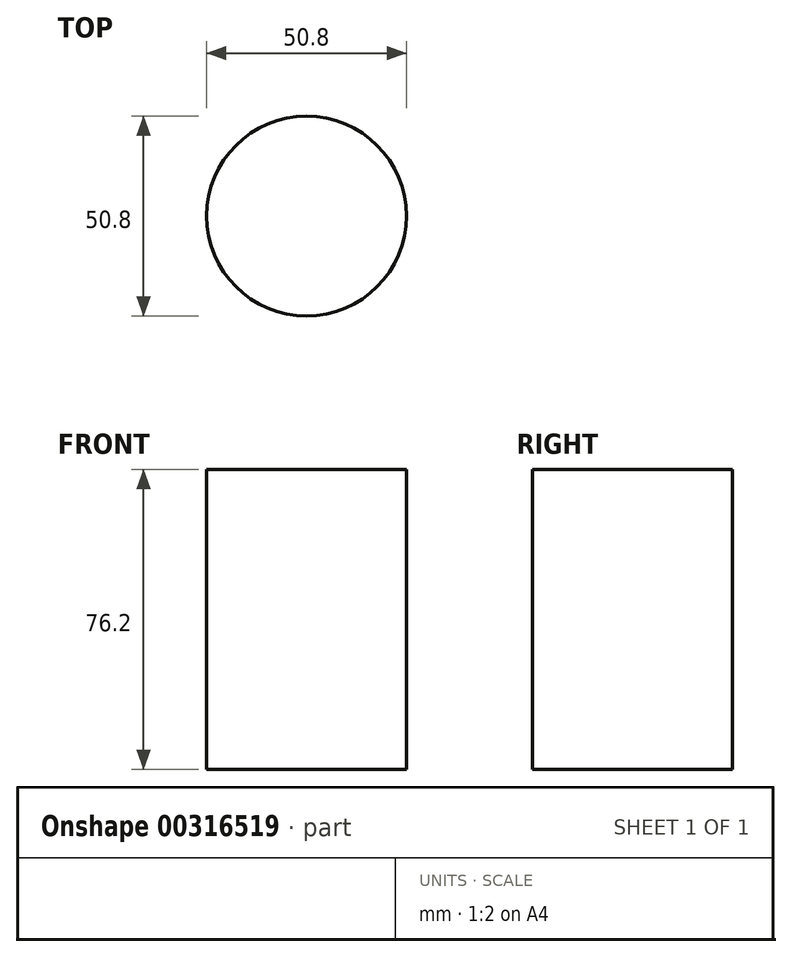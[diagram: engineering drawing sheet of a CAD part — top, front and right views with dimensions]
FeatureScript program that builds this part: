
annotation { "Feature Type Name" : "Feature", "Feature Type Description" : "" }
export const myFeature = defineFeature(function(context is Context, id is Id, definition is map)
    precondition{}
    {
        {
            var Q0;
            Q0=qCreatedBy(makeId("Top.planeOp"),FACE);
            var sketch = newSketch(context, id + "F0", { "sketchPlane" : qUnion([Q0])});
            skCircle(sketch, "E0", {"center": v(0, 0) * mm, "radius": 25.4 * mm});
            skCircle(sketch, "E1", {"center": v(0, 0) * mm, "radius": 63.5 * mm});
            skSolve(sketch);
        }
        {
            var Q0;
            Q0=makeQuery(id+"F0.imprint","IMPRINT",FACE,{"disambiguationData":[TD([[makeQuery(id+"F0.imprint","IMPRINT",EDGE,{"derivedFrom":sQuery(id+"F0.wireOp",EDGE,"E0")}),1.0]])]});
            extrude(context, id + "F1", {"entities" : qUnion([Q0]), "oppositeDirection" : true, "depth" : 76.2 * mm});
        }
    });
